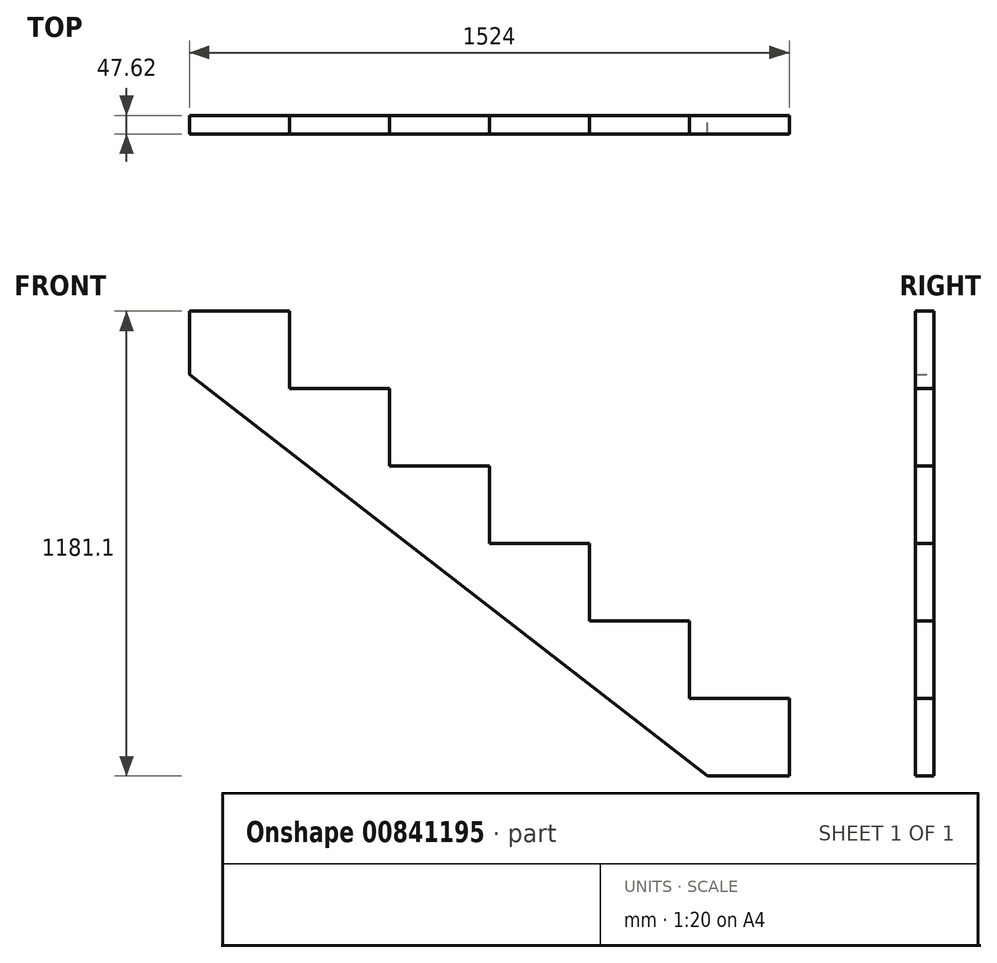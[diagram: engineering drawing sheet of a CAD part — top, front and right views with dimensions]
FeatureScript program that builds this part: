
annotation { "Feature Type Name" : "Feature", "Feature Type Description" : "" }
export const myFeature = defineFeature(function(context is Context, id is Id, definition is map)
    precondition{}
    {
        {
            var Q0;
            Q0=qCreatedBy(makeId("Front.planeOp"),FACE);
            var sketch = newSketch(context, id + "F0", { "sketchPlane" : qUnion([Q0])});
            skLineSegment(sketch, "E0", {"start": v(-762, 429.87) * mm, "end": v(554.68, -590.55) * mm});
            skLineSegment(sketch, "E1", {"start": v(-254, 393.7) * mm, "end": v(-508, 393.7) * mm});
            skLineSegment(sketch, "E2", {"start": v(-254, 393.7) * mm, "end": v(-254, 196.85) * mm});
            skLineSegment(sketch, "E3", {"start": v(0, 196.85) * mm, "end": v(-254, 196.85) * mm});
            skLineSegment(sketch, "E4", {"start": v(0, 196.85) * mm, "end": v(0, 0) * mm});
            skLineSegment(sketch, "E5", {"start": v(0, 0) * mm, "end": v(254, 0) * mm});
            skLineSegment(sketch, "E6", {"start": v(254, 0) * mm, "end": v(254, -196.85) * mm});
            skLineSegment(sketch, "E7", {"start": v(254, -196.85) * mm, "end": v(508, -196.85) * mm});
            skLineSegment(sketch, "E8", {"start": v(508, -196.85) * mm, "end": v(508, -393.7) * mm});
            skLineSegment(sketch, "E9", {"start": v(508, -393.7) * mm, "end": v(762, -393.7) * mm});
            skLineSegment(sketch, "E10", {"start": v(762, -393.7) * mm, "end": v(762, -590.55) * mm});
            skLineSegment(sketch, "E11", {"start": v(762, -590.55) * mm, "end": v(554.68, -590.55) * mm});
            skLineSegment(sketch, "E12", {"start": v(-508, 393.7) * mm, "end": v(-508, 590.55) * mm});
            skLineSegment(sketch, "E13", {"start": v(-508, 590.55) * mm, "end": v(-762, 590.55) * mm});
            skLineSegment(sketch, "E14", {"start": v(-762, 590.55) * mm, "end": v(-762, 429.87) * mm});
            skSolve(sketch);
        }
        {
            var Q0;
            Q0=makeQuery(id+"F0.imprint","IMPRINT",FACE,{"disambiguationData":[TD([[makeQuery(id+"F0.imprint","IMPRINT",EDGE,{"derivedFrom":sQuery(id+"F0.wireOp",EDGE,"E0")}),1.0]])]});
            extrude(context, id + "F1", {"entities" : qUnion([Q0]), "depth" : 47.62 * mm, "offsetDistance" : 25.4 * mm});
        }
    });
